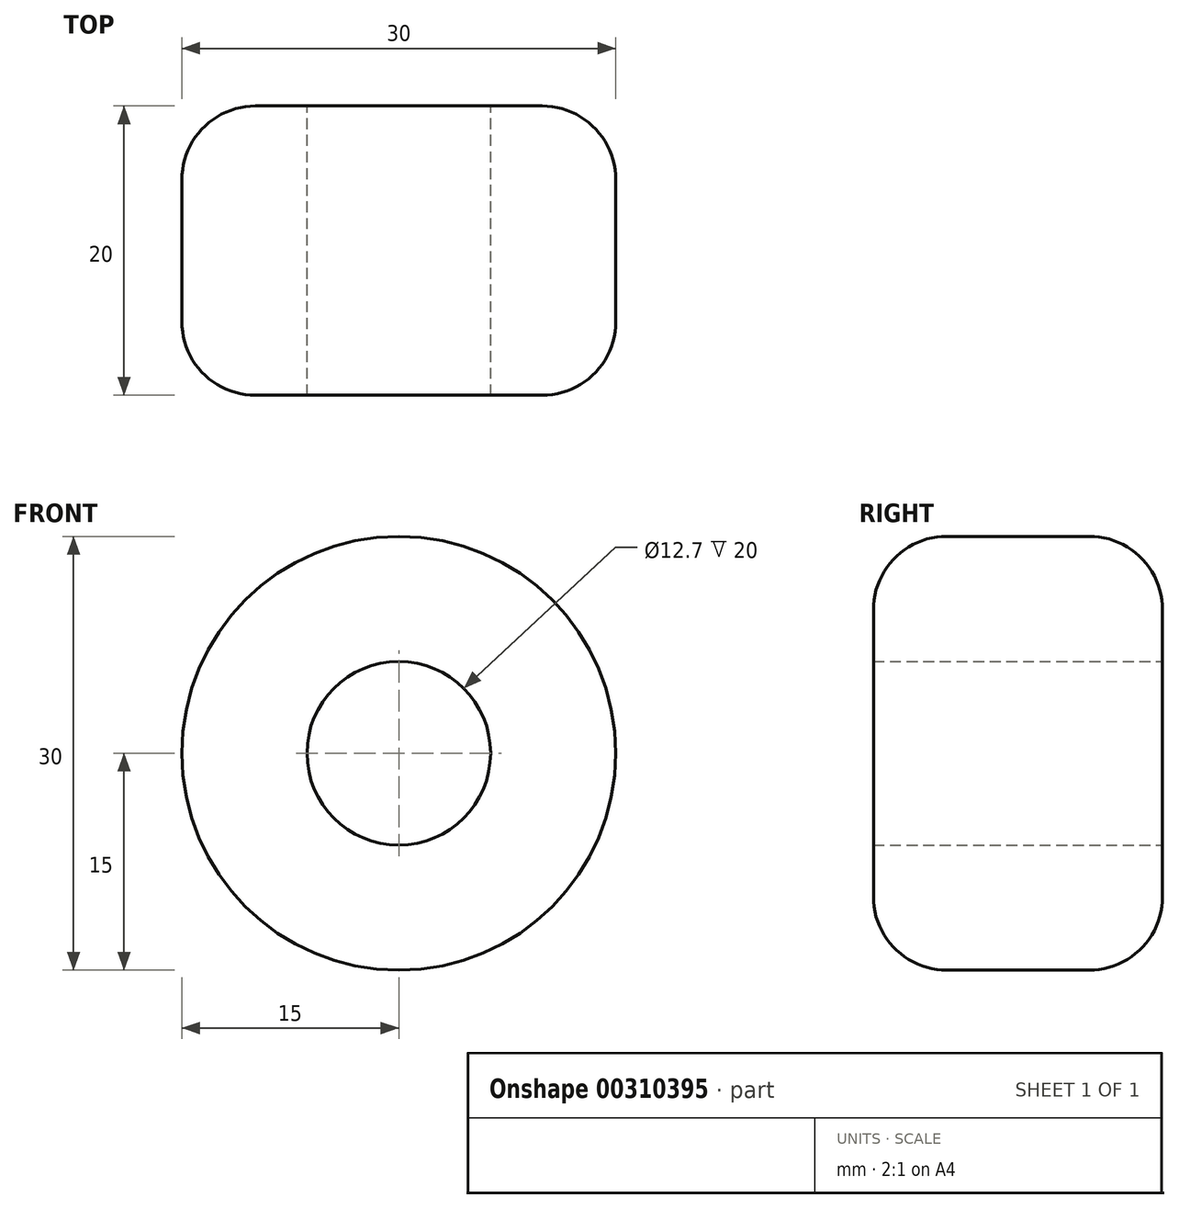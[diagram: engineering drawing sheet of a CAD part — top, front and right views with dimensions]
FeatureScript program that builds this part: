
annotation { "Feature Type Name" : "Feature", "Feature Type Description" : "" }
export const myFeature = defineFeature(function(context is Context, id is Id, definition is map)
    precondition{}
    {
        {
            var Q0;
            Q0=qCreatedBy(makeId("Front.planeOp"),FACE);
            var sketch = newSketch(context, id + "F0", { "sketchPlane" : qUnion([Q0])});
            skCircle(sketch, "E0", {"center": v(0, 0) * mm, "radius": 15 * mm});
            skSolve(sketch);
        }
        {
            var Q0;
            Q0=makeQuery(id+"F0.imprint","IMPRINT",FACE,{"disambiguationData":[TD([[makeQuery(id+"F0.imprint","IMPRINT",EDGE,{"derivedFrom":sQuery(id+"F0.wireOp",EDGE,"E0")}),1.0]])]});
            extrude(context, id + "F1", {"entities" : qUnion([Q0]), "depth" : 20 * mm});
        }
        {
            var Q0;
            Q0=makeQuery(id+"F1.opExtrude","CAP_EDGE",EDGE,{"disambiguationData":[OSD([sQuery(id+"F0.wireOp",EDGE,"E0")])],"isStart":false});
            fillet(context, id + "F2", {"entities" : qUnion([Q0]), "radius" : 5.08 * mm, "tangentPropagation" : true, "allowEdgeOverflow" : false});
        }
        {
            var Q0;
            Q0=makeQuery(id+"F1.opExtrude","SWEPT_FACE",FACE,{"disambiguationData":[OSD([sQuery(id+"F0.wireOp",EDGE,"E0")])]});
            fillet(context, id + "F3", {"entities" : qUnion([Q0]), "radius" : 5.08 * mm, "tangentPropagation" : true, "allowEdgeOverflow" : false});
        }
        {
            var Q0;
            Q0=qCreatedBy(makeId("Front.planeOp"),FACE);
            var sketch = newSketch(context, id + "F4", { "sketchPlane" : qUnion([Q0])});
            skCircle(sketch, "E1", {"center": v(0, 0) * mm, "radius": 6.35 * mm});
            skSolve(sketch);
        }
        {
            var Q0;
            Q0=sQuery(id+"F4.wireOp",VERTEX,"E1.center");
            var Q1;
            Q1=makeQuery(id+"F1.opExtrude","SWEPT_BODY",BODY,{"disambiguationData":[OSD([sQuery(id+"F0.wireOp",EDGE,"E0")])]});
            hole(context, id + "F5", {"style" : HoleStyle.SIMPLE, "endStyle" : HoleEndStyle.THROUGH, "oppositeDirection" : true, "holeDiameter" : 12.7 * mm, "tappedDepth" : 12.7 * mm, "tapClearance" : 3, "locations" : qUnion([Q0]), "scope" : qUnion([Q1])});
        }
    });
